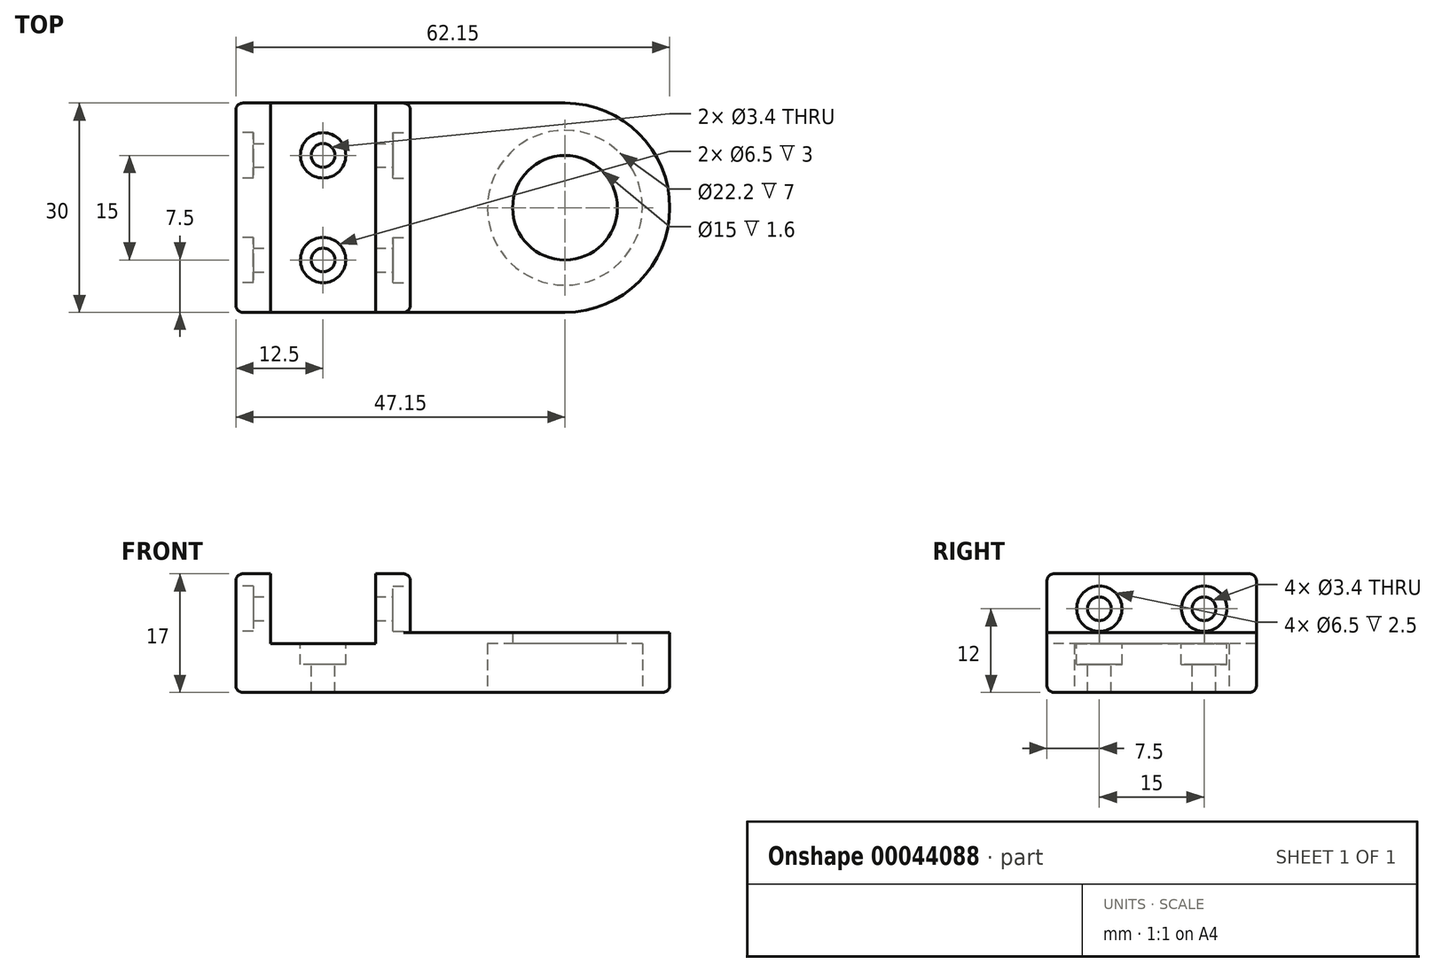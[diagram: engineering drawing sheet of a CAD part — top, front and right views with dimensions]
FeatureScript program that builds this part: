
annotation { "Feature Type Name" : "Feature", "Feature Type Description" : "" }
export const myFeature = defineFeature(function(context is Context, id is Id, definition is map)
    precondition{}
    {
        {
            var Q0;
            Q0=qCreatedBy(makeId("Top.planeOp"),FACE);
            var sketch = newSketch(context, id + "F0", { "sketchPlane" : qUnion([Q0])});
            skCircle(sketch, "E0", {"center": v(0, 0) * mm, "radius": 4 * mm, "construction": true});
            skCircle(sketch, "E1", {"center": v(0, 0) * mm, "radius": 11.1 * mm});
            skArc(sketch, "E2", {"start": v(0, -15) * mm, "mid": v(15, 0) * mm, "end": v(0, 15) * mm});
            skLineSegment(sketch, "E3", {"start": v(0, 15) * mm, "end": v(-47.15, 15) * mm});
            skLineSegment(sketch, "E4", {"start": v(0, -15) * mm, "end": v(-47.15, -15) * mm});
            skLineSegment(sketch, "E5", {"start": v(-47.15, 15) * mm, "end": v(-47.15, -15) * mm});
            skSolve(sketch);
        }
        {
            var Q0;
            Q0 = qSketchRegion(id + "F0", true);
            extrude(context, id + "F1", {"entities" : qUnion([Q0]), "depth" : 7 * mm});
        }
        {
            var Q0;
            Q0=makeQuery(id+"F1.opExtrude","CAP_FACE",FACE,{"disambiguationData":[OSD([sQuery(id+"F0.wireOp",EDGE,"E1"),sQuery(id+"F0.wireOp",EDGE,"E2"),sQuery(id+"F0.wireOp",EDGE,"E3"),sQuery(id+"F0.wireOp",EDGE,"E4"),sQuery(id+"F0.wireOp",EDGE,"E5")])],"isStart":false});
            var sketch = newSketch(context, id + "F2", { "sketchPlane" : qUnion([Q0])});
            skLineSegment(sketch, "E6.bottom", {"start": v(-47.15, 15) * mm, "end": v(-42.15, 15) * mm});
            skLineSegment(sketch, "E6.top", {"start": v(-47.15, -15) * mm, "end": v(-42.15, -15) * mm});
            skLineSegment(sketch, "E6.left", {"start": v(-47.15, 15) * mm, "end": v(-47.15, -15) * mm});
            skLineSegment(sketch, "E6.right", {"start": v(-42.15, 15) * mm, "end": v(-42.15, -15) * mm});
            skLineSegment(sketch, "E7.bottom", {"start": v(-27.15, 15) * mm, "end": v(-22.15, 15) * mm});
            skLineSegment(sketch, "E7.top", {"start": v(-27.15, -15) * mm, "end": v(-22.15, -15) * mm});
            skLineSegment(sketch, "E7.left", {"start": v(-27.15, 15) * mm, "end": v(-27.15, -15) * mm});
            skLineSegment(sketch, "E7.right", {"start": v(-22.15, 15) * mm, "end": v(-22.15, -15) * mm});
            skSolve(sketch);
        }
        {
            var Q0;
            Q0 = qSketchRegion(id + "F2", true);
            extrude(context, id + "F3", {"entities" : qUnion([Q0]), "operationType" : NewBodyOperationType.ADD, "depth" : 10 * mm});
        }
        {
            var Q0;
            Q0=makeQuery(id+"F3.opExtrude","SWEPT_FACE",FACE,{"disambiguationData":[OSD([sQuery(id+"F2.wireOp",EDGE,"E6.right")])]});
            var sketch = newSketch(context, id + "F4", { "sketchPlane" : qUnion([Q0])});
            skCircle(sketch, "E8", {"center": v(7.5, 12) * mm, "radius": 1.7 * mm});
            skPoint(sketch, "E8.centerSnap0", {"position": v(15, 12) * mm});
            skCircle(sketch, "E9", {"center": v(-7.5, 12) * mm, "radius": 1.7 * mm});
            skPoint(sketch, "E9.centerSnap0", {"position": v(-15, 12) * mm});
            skSolve(sketch);
        }
        {
            var Q0;
            Q0 = qSketchRegion(id + "F4", true);
            extrude(context, id + "F5", {"entities" : qUnion([Q0]), "operationType" : NewBodyOperationType.REMOVE, "endBound" : BoundingType.THROUGH_ALL, "oppositeDirection" : true, "depth" : 25 * mm});
        }
        {
            var Q0;
            Q0=makeQuery(id+"F3.boolean.opBoolean","MERGE",FACE,{"derivedFrom":[makeQuery(id+"F1.opExtrude","SWEPT_FACE",FACE,{"disambiguationData":[OSD([sQuery(id+"F0.wireOp",EDGE,"E5")])]}),makeQuery(id+"F3.opExtrude","SWEPT_FACE",FACE,{"disambiguationData":[OSD([sQuery(id+"F2.wireOp",EDGE,"E6.left")])]})]});
            var sketch = newSketch(context, id + "F6", { "sketchPlane" : qUnion([Q0])});
            skCircle(sketch, "E10", {"center": v(-7.5, 12) * mm, "radius": 3.25 * mm});
            skCircle(sketch, "E11", {"center": v(7.5, 12) * mm, "radius": 3.25 * mm});
            skSolve(sketch);
        }
        {
            var Q0;
            Q0 = qSketchRegion(id + "F6", true);
            extrude(context, id + "F7", {"entities" : qUnion([Q0]), "operationType" : NewBodyOperationType.REMOVE, "oppositeDirection" : true, "depth" : 2.5 * mm});
        }
        {
            var Q0;
            Q0=makeQuery(id+"F3.opExtrude","SWEPT_FACE",FACE,{"disambiguationData":[OSD([sQuery(id+"F2.wireOp",EDGE,"E7.right")])]});
            var sketch = newSketch(context, id + "F8", { "sketchPlane" : qUnion([Q0])});
            skCircle(sketch, "E12", {"center": v(7.5, 12) * mm, "radius": 1.7 * mm});
            skPoint(sketch, "E12.centerSnap0", {"position": v(15, 12) * mm});
            skCircle(sketch, "E13", {"center": v(-7.5, 12) * mm, "radius": 1.7 * mm});
            skPoint(sketch, "E13.centerSnap0", {"position": v(-15, 12) * mm});
            skSolve(sketch);
        }
        {
            var Q0;
            Q0 = qSketchRegion(id + "F8", true);
            extrude(context, id + "F9", {"entities" : qUnion([Q0]), "operationType" : NewBodyOperationType.REMOVE, "endBound" : BoundingType.THROUGH_ALL, "oppositeDirection" : true, "depth" : 25 * mm});
        }
        {
            var Q0;
            Q0=makeQuery(id+"F3.opExtrude","SWEPT_FACE",FACE,{"disambiguationData":[OSD([sQuery(id+"F2.wireOp",EDGE,"E7.right")])]});
            var sketch = newSketch(context, id + "F10", { "sketchPlane" : qUnion([Q0])});
            skCircle(sketch, "E14", {"center": v(7.5, 12) * mm, "radius": 3.25 * mm});
            skCircle(sketch, "E15", {"center": v(-7.5, 12) * mm, "radius": 3.25 * mm});
            skSolve(sketch);
        }
        {
            var Q0;
            Q0 = qSketchRegion(id + "F10", true);
            extrude(context, id + "F11", {"entities" : qUnion([Q0]), "operationType" : NewBodyOperationType.REMOVE, "oppositeDirection" : true, "depth" : 2.5 * mm});
        }
        {
            var Q0;
            {var subQ0=sQuery(id+"F0.wireOp",EDGE,"E4");var subQ1=sQuery(id+"F0.wireOp",EDGE,"E3");var subQ2=sQuery(id+"F0.wireOp",EDGE,"E2");var subQ3=sQuery(id+"F0.wireOp",EDGE,"E1");Q0=makeQuery(id+"F3.boolean.opBoolean","SPLIT",FACE,{"disambiguationData":[TD([makeQuery(id+"F1.opExtrude","SWEPT_FACE",FACE,{"disambiguationData":[OSD([subQ3])]})])],"derivedFrom":makeQuery(id+"F1.opExtrude","CAP_FACE",FACE,{"disambiguationData":[OSD([subQ3,subQ2,subQ1,subQ0,sQuery(id+"F0.wireOp",EDGE,"E5")])],"isStart":false})});}
            var sketch = newSketch(context, id + "F12", { "sketchPlane" : qUnion([Q0])});
            skLineSegment(sketch, "E16.0", {"start": v(0, 15) * mm, "end": v(-22.15, 15) * mm});
            skLineSegment(sketch, "E17.0", {"start": v(0, -15) * mm, "end": v(-22.15, -15) * mm});
            skArc(sketch, "E18.0", {"start": v(0, -15) * mm, "mid": v(15, 0) * mm, "end": v(0, 15) * mm});
            skLineSegment(sketch, "E19.0", {"start": v(-22.15, 15) * mm, "end": v(-22.15, -15) * mm});
            skCircle(sketch, "E20", {"center": v(0, 0) * mm, "radius": 7.5 * mm});
            skSolve(sketch);
        }
        {
            var Q0;
            Q0 = qSketchRegion(id + "F12", true);
            extrude(context, id + "F13", {"entities" : qUnion([Q0]), "operationType" : NewBodyOperationType.ADD, "depth" : 1.6 * mm});
        }
        {
            var Q0;
            Q0=makeQuery(id+"F1.opExtrude","CAP_EDGE",EDGE,{"disambiguationData":[OSD([sQuery(id+"F0.wireOp",EDGE,"E5")])],"isStart":true});
            var Q1;
            Q1=makeQuery(id+"F1.opExtrude","CAP_EDGE",EDGE,{"disambiguationData":[OSD([sQuery(id+"F0.wireOp",EDGE,"E4")])],"isStart":true});
            var Q2;
            Q2=makeQuery(id+"F1.opExtrude","CAP_EDGE",EDGE,{"disambiguationData":[OSD([sQuery(id+"F0.wireOp",EDGE,"E2")])],"isStart":true});
            var Q3;
            Q3=makeQuery(id+"F1.opExtrude","CAP_EDGE",EDGE,{"disambiguationData":[OSD([sQuery(id+"F0.wireOp",EDGE,"E3")])],"isStart":true});
            var Q4;
            Q4=makeQuery(id+"F3.boolean.opBoolean","MERGE",EDGE,{"derivedFrom":[makeQuery(id+"F1.opExtrude","SWEPT_EDGE",EDGE,{"disambiguationData":[OSD([sQuery(id+"F0.wireOp",EDGE,"E4"),sQuery(id+"F0.wireOp",EDGE,"E5")])]}),makeQuery(id+"F3.opExtrude","SWEPT_EDGE",EDGE,{"disambiguationData":[OSD([sQuery(id+"F2.wireOp",EDGE,"E6.top"),sQuery(id+"F2.wireOp",EDGE,"E6.left")])]})]});
            var Q5;
            Q5=makeQuery(id+"F3.boolean.opBoolean","MERGE",EDGE,{"derivedFrom":[makeQuery(id+"F1.opExtrude","SWEPT_EDGE",EDGE,{"disambiguationData":[OSD([sQuery(id+"F0.wireOp",EDGE,"E3"),sQuery(id+"F0.wireOp",EDGE,"E5")])]}),makeQuery(id+"F3.opExtrude","SWEPT_EDGE",EDGE,{"disambiguationData":[OSD([sQuery(id+"F2.wireOp",EDGE,"E6.bottom"),sQuery(id+"F2.wireOp",EDGE,"E6.left")])]})]});
            var Q6;
            Q6=makeQuery(id+"F3.opExtrude","CAP_EDGE",EDGE,{"disambiguationData":[OSD([sQuery(id+"F2.wireOp",EDGE,"E6.left")])],"isStart":false});
            var Q7;
            Q7=makeQuery(id+"F3.opExtrude","CAP_EDGE",EDGE,{"disambiguationData":[OSD([sQuery(id+"F2.wireOp",EDGE,"E7.right")])],"isStart":false});
            var Q8;
            Q8=makeQuery(id+"F3.opExtrude","SWEPT_EDGE",EDGE,{"disambiguationData":[OSD([sQuery(id+"F0.wireOp",EDGE,"E4"),sQuery(id+"F2.wireOp",EDGE,"E7.top"),sQuery(id+"F2.wireOp",EDGE,"E7.right")])]});
            var Q9;
            Q9=makeQuery(id+"F3.opExtrude","SWEPT_EDGE",EDGE,{"disambiguationData":[OSD([sQuery(id+"F0.wireOp",EDGE,"E3"),sQuery(id+"F2.wireOp",EDGE,"E7.bottom"),sQuery(id+"F2.wireOp",EDGE,"E7.right")])]});
            fillet(context, id + "F14", {"entities" : qUnion([Q0, Q1, Q2, Q3, Q4, Q5, Q6, Q7, Q8, Q9]), "radius" : 1 * mm, "tangentPropagation" : true, "allowEdgeOverflow" : false});
        }
        {
            var Q0;
            {var subQ0=sQuery(id+"F0.wireOp",EDGE,"E4");var subQ1=sQuery(id+"F0.wireOp",EDGE,"E3");Q0=makeQuery(id+"F3.boolean.opBoolean","SPLIT",FACE,{"disambiguationData":[TD([makeQuery(id+"F3.opExtrude","SWEPT_FACE",FACE,{"disambiguationData":[OSD([sQuery(id+"F2.wireOp",EDGE,"E6.right")])]})])],"derivedFrom":makeQuery(id+"F1.opExtrude","CAP_FACE",FACE,{"disambiguationData":[OSD([sQuery(id+"F0.wireOp",EDGE,"E1"),sQuery(id+"F0.wireOp",EDGE,"E2"),subQ1,subQ0,sQuery(id+"F0.wireOp",EDGE,"E5")])],"isStart":false})});}
            var sketch = newSketch(context, id + "F15", { "sketchPlane" : qUnion([Q0])});
            skCircle(sketch, "E21", {"center": v(-34.65, -7.5) * mm, "radius": 1.7 * mm});
            skPoint(sketch, "E21.centerSnap0", {"position": v(-34.65, -15) * mm});
            skCircle(sketch, "E22", {"center": v(-34.65, 7.5) * mm, "radius": 1.7 * mm});
            skPoint(sketch, "E22.centerSnap0", {"position": v(-34.65, 15) * mm});
            skSolve(sketch);
        }
        {
            var Q0;
            Q0 = qSketchRegion(id + "F15", true);
            extrude(context, id + "F16", {"entities" : qUnion([Q0]), "operationType" : NewBodyOperationType.REMOVE, "endBound" : BoundingType.THROUGH_ALL, "oppositeDirection" : true, "depth" : 25 * mm});
        }
        {
            var Q0;
            {var subQ0=sQuery(id+"F0.wireOp",EDGE,"E4");var subQ1=sQuery(id+"F0.wireOp",EDGE,"E3");Q0=makeQuery(id+"F3.boolean.opBoolean","SPLIT",FACE,{"disambiguationData":[TD([makeQuery(id+"F3.opExtrude","SWEPT_FACE",FACE,{"disambiguationData":[OSD([sQuery(id+"F2.wireOp",EDGE,"E6.right")])]})])],"derivedFrom":makeQuery(id+"F1.opExtrude","CAP_FACE",FACE,{"disambiguationData":[OSD([sQuery(id+"F0.wireOp",EDGE,"E1"),sQuery(id+"F0.wireOp",EDGE,"E2"),subQ1,subQ0,sQuery(id+"F0.wireOp",EDGE,"E5")])],"isStart":false})});}
            var sketch = newSketch(context, id + "F17", { "sketchPlane" : qUnion([Q0])});
            skCircle(sketch, "E23", {"center": v(-34.65, -7.5) * mm, "radius": 3.25 * mm});
            skCircle(sketch, "E24", {"center": v(-34.65, 7.5) * mm, "radius": 3.25 * mm});
            skSolve(sketch);
        }
        {
            var Q0;
            Q0 = qSketchRegion(id + "F17", true);
            extrude(context, id + "F18", {"entities" : qUnion([Q0]), "operationType" : NewBodyOperationType.REMOVE, "oppositeDirection" : true, "depth" : 3 * mm});
        }
        {
            var Q0;
            Q0=makeQuery(id+"F3.opExtrude","CAP_EDGE",EDGE,{"disambiguationData":[OSD([sQuery(id+"F2.wireOp",EDGE,"E6.bottom")])],"isStart":false});
            var Q1;
            Q1=makeQuery(id+"F3.opExtrude","CAP_EDGE",EDGE,{"disambiguationData":[OSD([sQuery(id+"F2.wireOp",EDGE,"E7.bottom")])],"isStart":false});
            var Q2;
            Q2=makeQuery(id+"F3.opExtrude","CAP_EDGE",EDGE,{"disambiguationData":[OSD([sQuery(id+"F2.wireOp",EDGE,"E7.top")])],"isStart":false});
            var Q3;
            Q3=makeQuery(id+"F3.opExtrude","CAP_EDGE",EDGE,{"disambiguationData":[OSD([sQuery(id+"F2.wireOp",EDGE,"E6.top")])],"isStart":false});
            fillet(context, id + "F19", {"entities" : qUnion([Q0, Q1, Q2, Q3]), "radius" : 1 * mm, "tangentPropagation" : true, "allowEdgeOverflow" : false});
        }
    });
